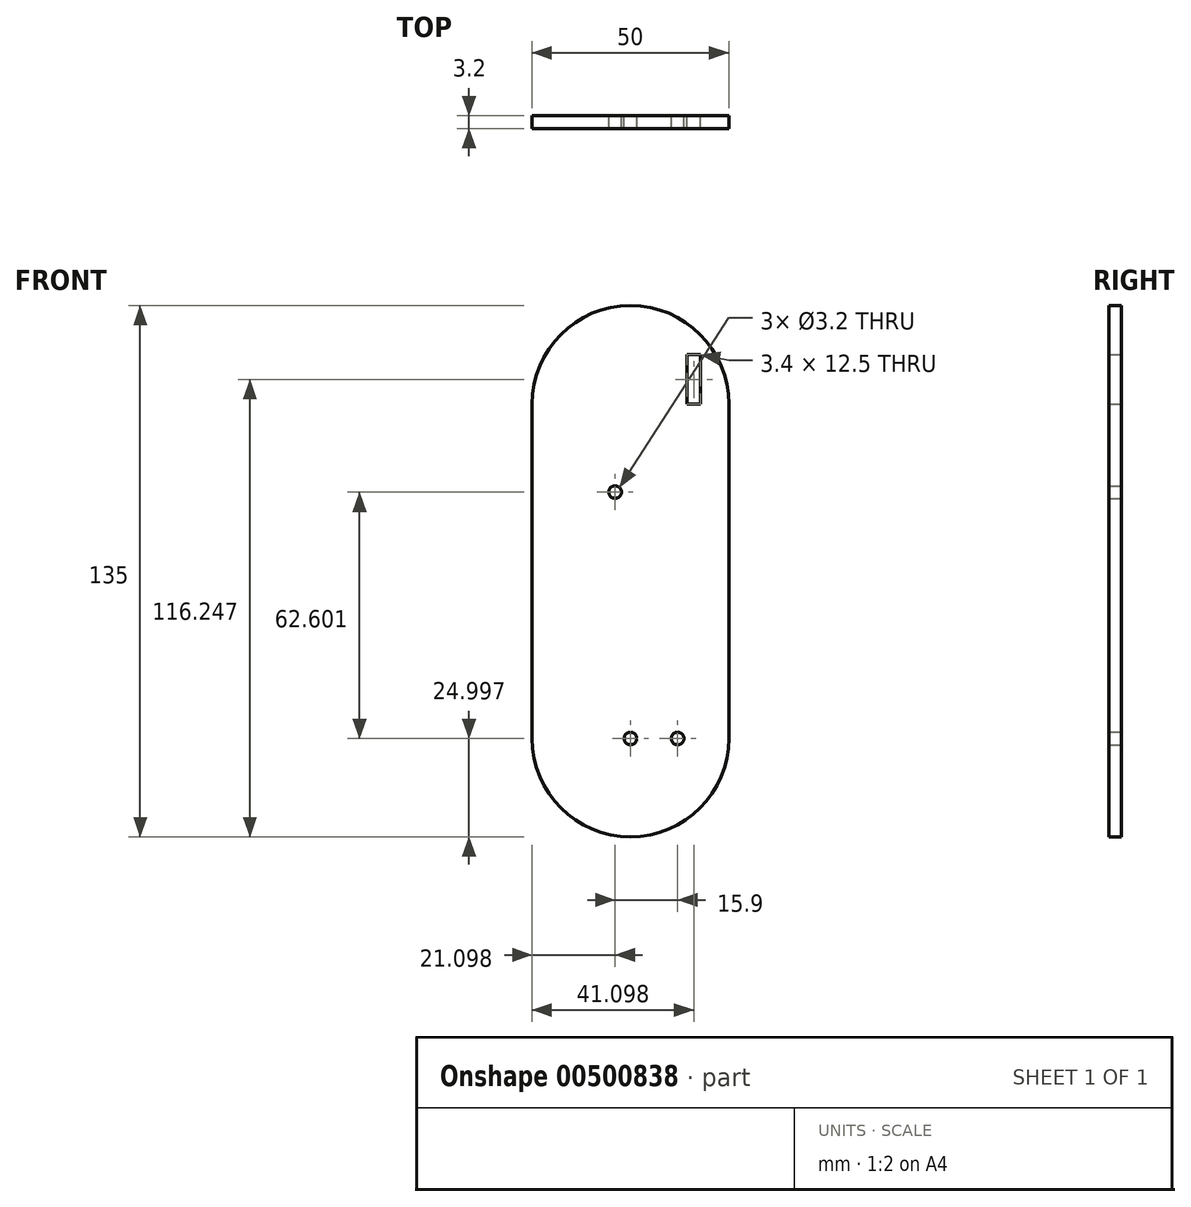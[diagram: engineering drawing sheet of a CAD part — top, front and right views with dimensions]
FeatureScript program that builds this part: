
annotation { "Feature Type Name" : "Feature", "Feature Type Description" : "" }
export const myFeature = defineFeature(function(context is Context, id is Id, definition is map)
    precondition{}
    {
        {
            var Q0;
            Q0=qCreatedBy(makeId("Front.planeOp"),FACE);
            var sketch = newSketch(context, id + "F0", { "sketchPlane" : qUnion([Q0])});
            skLineSegment(sketch, "E0", {"start": v(-25.05, -22.07) * mm, "end": v(-25.05, 62.93) * mm});
            skLineSegment(sketch, "E1", {"start": v(24.95, 62.93) * mm, "end": v(24.95, -22.07) * mm});
            skCircle(sketch, "E2", {"center": v(11.95, -22.07) * mm, "radius": 1.6 * mm});
            skArc(sketch, "E3", {"start": v(-25.05, -22.07) * mm, "mid": v(-0.05, -47.07) * mm, "end": v(24.95, -22.07) * mm});
            skArc(sketch, "E4", {"start": v(24.95, 62.93) * mm, "mid": v(-0.05, 87.93) * mm, "end": v(-25.05, 62.93) * mm});
            skCircle(sketch, "E5", {"center": v(-0.05, -22.07) * mm, "radius": 1.6 * mm});
            skPoint(sketch, "E6", {"position": v(-25.05, 20.43) * mm});
            skLineSegment(sketch, "E7.bottom", {"start": v(14.35, 62.93) * mm, "end": v(17.75, 62.93) * mm});
            skLineSegment(sketch, "E7.top", {"start": v(14.35, 75.43) * mm, "end": v(17.75, 75.43) * mm});
            skLineSegment(sketch, "E7.left", {"start": v(14.35, 62.93) * mm, "end": v(14.35, 75.43) * mm});
            skLineSegment(sketch, "E7.right", {"start": v(10.25, 62.93) * mm, "end": v(10.25, 75.56) * mm});
            skLineSegment(sketch, "E8", {"start": v(11.95, -22.07) * mm, "end": v(6.15, -22.07) * mm, "construction": true});
            skPoint(sketch, "E9", {"position": v(10.35, -22.07) * mm});
            skLineSegment(sketch, "E10", {"start": v(10.35, -22.07) * mm, "end": v(10.35, 82.54) * mm, "construction": true});
            skPoint(sketch, "E11", {"position": v(10.35, 62.93) * mm});
            skLineSegment(sketch, "E12", {"start": v(10.35, 20.43) * mm, "end": v(8.75, 20.43) * mm});
            skLineSegment(sketch, "E13", {"start": v(8.75, 20.43) * mm, "end": v(8.75, 78.96) * mm});
            skLineSegment(sketch, "E14", {"start": v(17.75, 62.93) * mm, "end": v(17.75, 75.43) * mm});
            skPoint(sketch, "E15", {"position": v(8.75, 62.93) * mm});
            skLineSegment(sketch, "E16", {"start": v(-0.05, 62.93) * mm, "end": v(0, 18.73) * mm, "construction": true});
            skPoint(sketch, "E17", {"position": v(-0.03, 40.83) * mm});
            skCircle(sketch, "E18", {"center": v(-3.95, 40.53) * mm, "radius": 1.6 * mm});
            skSolve(sketch);
        }
        {
            var Q0;
            Q0 = qSketchRegion(id + "F0", true);
            extrude(context, id + "F1", {"entities" : qUnion([Q0]), "depth" : 3.2 * mm, "offsetDistance" : 25 * mm});
        }
    });
